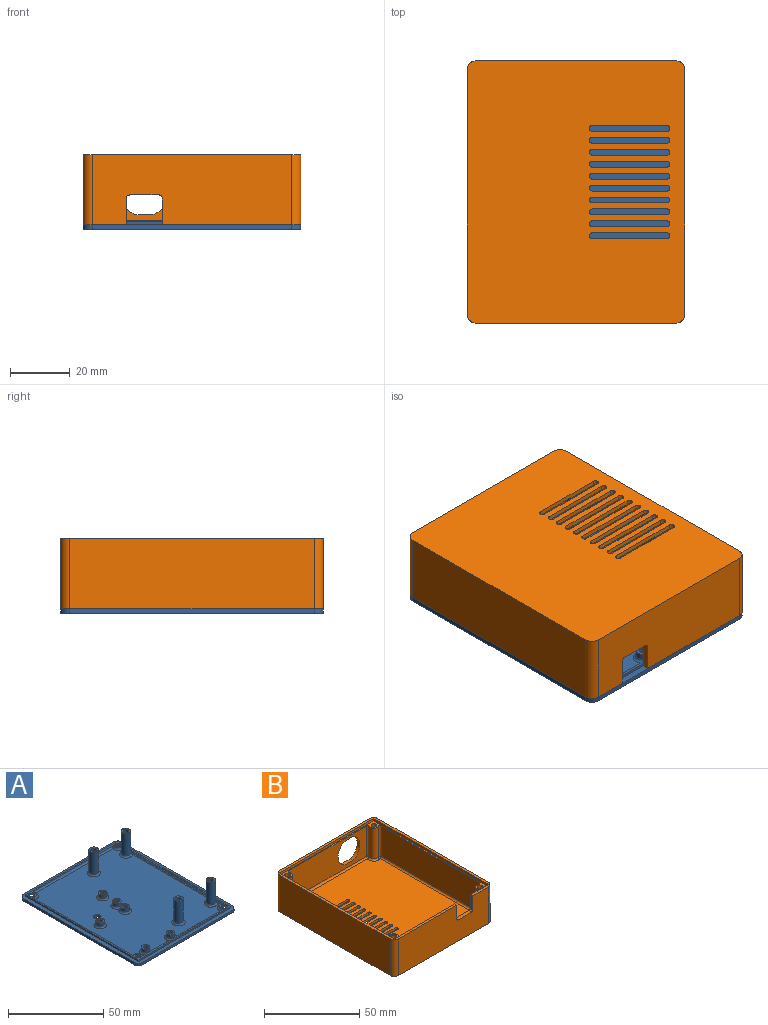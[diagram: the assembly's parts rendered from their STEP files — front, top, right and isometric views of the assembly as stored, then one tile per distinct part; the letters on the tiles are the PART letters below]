
ASSEMBLY  parts=2 mates=1
PART A: 83 faces, bbox 73x88x16.5 mm
  f0: plane 88x73mm, normal (0,0,1), area 620.3mm2, adj f2,f3,f4,f6,f9,f10,f11,f12
  f1: plane 80x65mm, normal (0,0,1), area 4801mm2, adj f5,f57,f58,f59,f60,f61,f62,f63
  f2: plane 82x1.5mm, normal (1,0,0), area 123mm2, adj f0,f7,f53,f56
  f3: plane 67x1.5mm, normal (0,1,0), area 100.5mm2, adj f0,f7,f53,f54
  f4: plane 82x1.5mm, normal (-1,0,0), area 123mm2, adj f0,f7,f54,f55
  f5: cylinder r=2mm len=4mm, axis (0,0,-1), area 18.8mm2, adj f1,f7
  f6: plane 67x1.5mm, normal (0,-1,0), area 100.5mm2, adj f0,f7,f55,f56
  f7: plane 88x73mm, normal (0,0,-1), area 6249.8mm2, adj f2,f3,f4,f5,f6,f53,f54,f55
  f8: plane 84x69mm, normal (0,0,1), area 328.5mm2, adj f9,f10,f11,f12,f57,f58,f59,f62
  f9: plane 84x1mm, normal (-1,0,0), area 84mm2, adj f0,f8,f10,f12
  f10: plane 69x1mm, normal (0,1,0), area 69mm2, adj f0,f8,f9,f11
  f11: plane 84x1mm, normal (1,0,0), area 84mm2, adj f0,f8,f10,f12
  f12: plane 69x1mm, normal (0,-1,0), area 69mm2, adj f0,f8,f9,f11
  f13: plane 4.5x4.5mm, normal (0,0,1), area 11mm2, adj f14,f15
  f14: cylinder r=1.25mm len=3mm, axis (0,0,-1), area 23.6mm2, adj f13,f16
  f15: cylinder r=2.25mm len=4.5mm, axis (0,0,-1), area 28.3mm2, adj f13,f74
  f16: plane 2.5x2.5mm, normal (0,0,1), area 4.9mm2, adj f14
  f17: plane 4.5x4.5mm, normal (0,0,1), area 11mm2, adj f18,f19
  f18: cylinder r=1.25mm len=3mm, axis (0,0,-1), area 23.6mm2, adj f17,f20
  f19: cylinder r=2.25mm len=4.5mm, axis (0,0,-1), area 28.3mm2, adj f17,f71
  f20: plane 2.5x2.5mm, normal (0,0,1), area 4.9mm2, adj f18
  f21: plane 4.5x4.5mm, normal (0,0,1), area 11mm2, adj f22,f23
  f22: cylinder r=1.25mm len=3mm, axis (0,0,-1), area 23.6mm2, adj f21,f24
  f23: cylinder r=2.25mm len=4.5mm, axis (0,0,-1), area 28.3mm2, adj f21,f61
  f24: plane 2.5x2.5mm, normal (0,0,1), area 4.9mm2, adj f22
  f25: plane 4.5x4.5mm, normal (0,0,1), area 11mm2, adj f26,f27
  f26: cylinder r=1.25mm len=3mm, axis (0,0,-1), area 23.6mm2, adj f25,f28
  f27: cylinder r=2.25mm len=4.5mm, axis (0,0,-1), area 28.3mm2, adj f25,f60
  f28: plane 2.5x2.5mm, normal (0,0,1), area 4.9mm2, adj f26
  f29: plane 4.5x4.5mm, normal (0,0,1), area 11mm2, adj f30,f31
  f30: cylinder r=1.25mm len=3mm, axis (0,0,-1), area 23.6mm2, adj f29,f32
  f31: cylinder r=2.25mm len=4.5mm, axis (0,0,-1), area 28.3mm2, adj f29,f73
  f32: plane 2.5x2.5mm, normal (0,0,1), area 4.9mm2, adj f30
  f33: plane 4.5x4.5mm, normal (0,0,1), area 11mm2, adj f34,f35
  f34: cylinder r=1.25mm len=3mm, axis (0,0,-1), area 23.6mm2, adj f33,f36
  f35: cylinder r=2.25mm len=4.5mm, axis (0,0,-1), area 28.3mm2, adj f33,f72
  f36: plane 2.5x2.5mm, normal (0,0,1), area 4.9mm2, adj f34
  f37: plane 5x5mm, normal (0,0,1), area 12.6mm2, adj f38,f39
  f38: cylinder r=1.5mm len=15mm, axis (0,0,-1), area 141.4mm2, adj f37,f40
  f39: cylinder r=2.5mm len=14mm, axis (0,0,-1), area 219.9mm2, adj f37,f70
  f40: plane 3x3mm, normal (0,0,1), area 7.1mm2, adj f38
  f41: plane 5x5mm, normal (0,0,1), area 12.6mm2, adj f42,f43
  f42: cylinder r=1.5mm len=15mm, axis (0,0,-1), area 141.4mm2, adj f41,f44
  f43: cylinder r=2.5mm len=14mm, axis (0,0,-1), area 219.9mm2, adj f41,f64
  f44: plane 3x3mm, normal (0,0,1), area 7.1mm2, adj f42
  f45: plane 5x5mm, normal (0,0,1), area 12.6mm2, adj f46,f47
  f46: cylinder r=1.5mm len=15mm, axis (0,0,-1), area 141.4mm2, adj f45,f48
  f47: cylinder r=2.5mm len=14mm, axis (0,0,-1), area 219.9mm2, adj f45,f69
  f48: plane 3x3mm, normal (0,0,1), area 7.1mm2, adj f46
  f49: plane 5x5mm, normal (0,0,1), area 12.6mm2, adj f50,f51
  f50: cylinder r=1.5mm len=15mm, axis (0,0,-1), area 141.4mm2, adj f49,f52
  f51: cylinder r=2.5mm len=14mm, axis (0,0,-1), area 219.9mm2, adj f49,f68
  f52: plane 3x3mm, normal (0,0,1), area 7.1mm2, adj f50
  f53: cylinder r=3mm len=3mm, axis (0,0,-1), area 7.1mm2, adj f0,f2,f3,f7
  f54: cylinder r=3mm len=3mm, axis (0,0,1), area 7.1mm2, adj f0,f3,f4,f7
  f55: cylinder r=3mm len=3mm, axis (0,0,-1), area 7.1mm2, adj f0,f4,f6,f7
  f56: cylinder r=3mm len=3mm, axis (0,0,1), area 7.1mm2, adj f0,f2,f6,f7
  f57: cylinder r=1mm len=75mm, axis (0,-1,0), area 115.5mm2, adj f1,f8,f58,f59
  f58: torus R=3.5mm, axis (0,0,1), area 10.5mm2, adj f1,f8,f57,f62
  f59: torus R=3.5mm, axis (0,0,1), area 10.5mm2, adj f1,f8,f57,f63
  f60: torus R=3.25mm, axis (0,0,1), area 22mm2, adj f1,f27,f63
  f61: torus R=3.25mm, axis (0,0,1), area 22mm2, adj f1,f23,f63
  f62: cylinder r=1mm len=60mm, axis (-1,0,0), area 91.9mm2, adj f1,f8,f58,f65
  f63: cylinder r=1mm len=60mm, axis (1,0,0), area 85.1mm2, adj f1,f8,f59,f60,f61,f66
  f64: torus R=3.5mm, axis (0,0,1), area 26.9mm2, adj f1,f43,f67
  f65: torus R=3.5mm, axis (0,0,1), area 10.5mm2, adj f1,f8,f62,f67
  f66: torus R=3.5mm, axis (0,0,1), area 10.5mm2, adj f1,f8,f63,f67
  f67: cylinder r=1mm len=75mm, axis (0,1,0), area 112.9mm2, adj f1,f8,f64,f65,f66,f68
  f68: torus R=3.5mm, axis (0,0,1), area 26.9mm2, adj f1,f51,f67
  f69: torus R=3.5mm, axis (0,0,1), area 28.3mm2, adj f1,f47
  f70: torus R=3.5mm, axis (0,0,1), area 28.3mm2, adj f1,f39
  f71: torus R=3.25mm, axis (0,0,1), area 25.7mm2, adj f1,f19,f72
  f72: torus R=3.25mm, axis (0,0,1), area 25.7mm2, adj f1,f35,f71
  f73: torus R=3.25mm, axis (0,0,1), area 25.8mm2, adj f1,f31
  f74: torus R=3.25mm, axis (0,0,1), area 25.8mm2, adj f1,f15
  f75: cylinder r=1.55mm len=3.1mm, axis (0,0,-1), area 2.5mm2, adj f8,f76
  f76: cone r=1.55mm half-angle=41deg, axis (0,0,-1), area 47.2mm2, adj f7,f75
  f77: cylinder r=1.55mm len=3.1mm, axis (0,0,-1), area 2.5mm2, adj f8,f78
  f78: cone r=1.55mm half-angle=41deg, axis (0,0,-1), area 47.2mm2, adj f7,f77
  f79: cylinder r=1.55mm len=3.1mm, axis (0,0,-1), area 2.5mm2, adj f8,f80
  f80: cone r=1.55mm half-angle=41deg, axis (0,0,-1), area 47.2mm2, adj f7,f79
  f81: cylinder r=1.55mm len=3.1mm, axis (0,0,-1), area 2.5mm2, adj f8,f82
  f82: cone r=1.55mm half-angle=41deg, axis (0,0,-1), area 47.2mm2, adj f7,f81
PART B: 106 faces, bbox 73x88x23.5 mm
  f0: plane 88x73mm, normal (0,0,-1), area 5884.9mm2, adj f7,f8,f9,f10,f33,f34,f35,f36
  f1: plane 82x67mm, normal (0,0,1), area 4874.4mm2, adj f45,f48,f49,f52,f53,f56,f57,f60
  f2: plane 88x73mm, normal (0,0,1), area 448.3mm2, adj f3,f4,f7,f8,f9,f10,f11,f12
  f3: plane 13x1.5mm, normal (0,1,0), area 19.5mm2, adj f2,f6,f13,f61
  f4: plane 45x1.5mm, normal (0,1,0), area 67.5mm2, adj f2,f6,f11,f62
  f5: plane 57.68x19.5mm, normal (0,1,0), area 1023.1mm2, adj f6,f37,f44,f45,f61,f62,f63,f64
  f6: plane 85x70mm, normal (0,0,1), area 211.7mm2, adj f3,f4,f5,f11,f12,f13,f14,f15
  f7: plane 82x23.5mm, normal (1,0,0), area 1927mm2, adj f0,f2,f33,f36
  f8: plane 67x23.5mm, normal (0,1,0), area 1370.9mm2, adj f0,f2,f29,f30,f31,f32,f33,f34
  f9: plane 82x23.5mm, normal (-1,0,0), area 1927mm2, adj f0,f2,f34,f35
  f10: plane 67x23.5mm, normal (0,-1,0), area 1454.9mm2, adj f0,f2,f35,f36,f61,f62,f63,f64
  f11: plane 85x1.5mm, normal (1,0,0), area 127.5mm2, adj f2,f4,f6,f12
  f12: plane 70x1.5mm, normal (0,-1,0), area 105mm2, adj f2,f6,f11,f13
  f13: plane 85x1.5mm, normal (-1,0,0), area 127.5mm2, adj f2,f3,f6,f12
  f14: cylinder r=1.5mm len=20.5mm, axis (0,0,-1), area 193.2mm2, adj f6,f28
  f15: cylinder r=1.5mm len=20.5mm, axis (0,0,-1), area 193.2mm2, adj f6,f27
  f16: cylinder r=2.5mm len=19.5mm, axis (0,0,-1), area 119.8mm2, adj f6,f43,f44,f48
  f17: plane 72.68x19.5mm, normal (-1,0,0), area 1417.2mm2, adj f6,f42,f43,f52
  f18: cylinder r=2.5mm len=19.5mm, axis (0,0,-1), area 119.8mm2, adj f6,f41,f42,f56
  f19: plane 57.68x19.5mm, normal (0,-1,0), area 921mm2, adj f6,f29,f30,f31,f32,f40,f41,f60
  f20: cylinder r=2.5mm len=19.5mm, axis (0,0,-1), area 119.8mm2, adj f6,f39,f40,f57
  f21: plane 72.68x19.5mm, normal (1,0,0), area 1417.2mm2, adj f6,f38,f39,f53
  f22: cylinder r=2.5mm len=19.5mm, axis (0,0,-1), area 119.8mm2, adj f6,f37,f38,f49
  f23: cylinder r=1.5mm len=20.5mm, axis (0,0,-1), area 193.2mm2, adj f6,f26
  f24: cylinder r=1.5mm len=20.5mm, axis (0,0,-1), area 193.2mm2, adj f6,f25
  f25: plane 3x3mm, normal (0,0,1), area 7.1mm2, adj f24
  f26: plane 3x3mm, normal (0,0,1), area 7.1mm2, adj f23
  f27: plane 3x3mm, normal (0,0,1), area 7.1mm2, adj f15
  f28: plane 3x3mm, normal (0,0,1), area 7.1mm2, adj f14
  f29: cylinder r=8.12mm len=15.25mm, axis (0,1,0), area 39.6mm2, adj f8,f19,f30,f31
  f30: plane 5.61x2mm, normal (0,0,1), area 11.2mm2, adj f8,f19,f29,f32
  f31: plane 5.61x2mm, normal (0,0,-1), area 11.2mm2, adj f8,f19,f29,f32
  f32: cylinder r=8.12mm len=15.25mm, axis (0,1,0), area 39.6mm2, adj f8,f19,f30,f31
  f33: cylinder r=3mm len=23.5mm, axis (0,0,-1), area 110.7mm2, adj f0,f2,f7,f8
  f34: cylinder r=3mm len=23.5mm, axis (0,0,1), area 110.7mm2, adj f0,f2,f8,f9
  f35: cylinder r=3mm len=23.5mm, axis (0,0,-1), area 110.7mm2, adj f0,f2,f9,f10
  f36: cylinder r=3mm len=23.5mm, axis (0,0,1), area 110.7mm2, adj f0,f2,f7,f10
  f37: cylinder r=1mm len=19.5mm, axis (0,0,-1), area 39.3mm2, adj f5,f6,f22,f47
  f38: cylinder r=1mm len=19.5mm, axis (0,0,-1), area 39.3mm2, adj f6,f21,f22,f51
  f39: cylinder r=1mm len=19.5mm, axis (0,0,-1), area 39.3mm2, adj f6,f20,f21,f55
  f40: cylinder r=1mm len=19.5mm, axis (0,0,-1), area 39.3mm2, adj f6,f19,f20,f59
  f41: cylinder r=1mm len=19.5mm, axis (0,0,-1), area 39.3mm2, adj f6,f18,f19,f58
  f42: cylinder r=1mm len=19.5mm, axis (0,0,-1), area 39.3mm2, adj f6,f17,f18,f54
  f43: cylinder r=1mm len=19.5mm, axis (0,0,-1), area 39.3mm2, adj f6,f16,f17,f50
  f44: cylinder r=1mm len=19.5mm, axis (0,0,-1), area 39.3mm2, adj f5,f6,f16,f46
  f45: cylinder r=1mm len=57.68mm, axis (1,0,0), area 90.6mm2, adj f1,f5,f46,f47
  f46: sphere r=1mm, area 2mm2, adj f44,f45,f48
  f47: sphere r=1mm, area 2mm2, adj f37,f45,f49
  f48: torus R=3.5mm, axis (0,0,1), area 11mm2, adj f1,f16,f46,f50
  f49: torus R=3.5mm, axis (0,0,1), area 11mm2, adj f1,f22,f47,f51
  f50: sphere r=1mm, area 2mm2, adj f43,f48,f52
  f51: sphere r=1mm, area 2mm2, adj f38,f49,f53
  f52: cylinder r=1mm len=72.68mm, axis (0,1,0), area 114.2mm2, adj f1,f17,f50,f54
  f53: cylinder r=1mm len=72.68mm, axis (0,-1,0), area 114.2mm2, adj f1,f21,f51,f55
  f54: sphere r=1mm, area 2mm2, adj f42,f52,f56
  f55: sphere r=1mm, area 2mm2, adj f39,f53,f57
  f56: torus R=3.5mm, axis (0,0,1), area 11mm2, adj f1,f18,f54,f58
  f57: torus R=3.5mm, axis (0,0,1), area 11mm2, adj f1,f20,f55,f59
  f58: sphere r=1mm, area 2mm2, adj f41,f56,f60
  f59: sphere r=1mm, area 2mm2, adj f40,f57,f60
  f60: cylinder r=1mm len=57.68mm, axis (-1,0,0), area 90.6mm2, adj f1,f19,f58,f59
  f61: plane 9x2mm, normal (-1,0,0), area 17.2mm2, adj f2,f3,f5,f6,f10,f65
  f62: plane 9x2mm, normal (1,0,0), area 17.2mm2, adj f2,f4,f5,f6,f10,f64
  f63: plane 10x2mm, normal (0,0,1), area 20mm2, adj f5,f10,f64,f65
  f64: cylinder r=1mm len=2mm, axis (0,1,0), area 3.1mm2, adj f5,f10,f62,f63
  f65: cylinder r=1mm len=2mm, axis (0,1,0), area 3.1mm2, adj f5,f10,f61,f63
  f66: cylinder r=1mm len=2mm, axis (0,0,1), area 4.7mm2, adj f0,f1,f67,f69
  f67: plane 25x1.5mm, normal (0,-1,0), area 37.5mm2, adj f0,f1,f66,f68
  f68: cylinder r=1mm len=2mm, axis (0,0,1), area 4.7mm2, adj f0,f1,f67,f69
  f69: plane 25x1.5mm, normal (0,1,0), area 37.5mm2, adj f0,f1,f66,f68
  f70: cylinder r=1mm len=2mm, axis (0,0,1), area 4.7mm2, adj f0,f1,f71,f73
  f71: plane 25x1.5mm, normal (0,-1,0), area 37.5mm2, adj f0,f1,f70,f72
  f72: cylinder r=1mm len=2mm, axis (0,0,1), area 4.7mm2, adj f0,f1,f71,f73
  f73: plane 25x1.5mm, normal (0,1,0), area 37.5mm2, adj f0,f1,f70,f72
  f74: cylinder r=1mm len=2mm, axis (0,0,1), area 4.7mm2, adj f0,f1,f75,f77
  f75: plane 25x1.5mm, normal (0,-1,0), area 37.5mm2, adj f0,f1,f74,f76
  f76: cylinder r=1mm len=2mm, axis (0,0,1), area 4.7mm2, adj f0,f1,f75,f77
  f77: plane 25x1.5mm, normal (0,1,0), area 37.5mm2, adj f0,f1,f74,f76
  f78: cylinder r=1mm len=2mm, axis (0,0,1), area 4.7mm2, adj f0,f1,f79,f81
  f79: plane 25x1.5mm, normal (0,-1,0), area 37.5mm2, adj f0,f1,f78,f80
  f80: cylinder r=1mm len=2mm, axis (0,0,1), area 4.7mm2, adj f0,f1,f79,f81
  f81: plane 25x1.5mm, normal (0,1,0), area 37.5mm2, adj f0,f1,f78,f80
  f82: cylinder r=1mm len=2mm, axis (0,0,1), area 4.7mm2, adj f0,f1,f83,f85
  f83: plane 25x1.5mm, normal (0,-1,0), area 37.5mm2, adj f0,f1,f82,f84
  f84: cylinder r=1mm len=2mm, axis (0,0,1), area 4.7mm2, adj f0,f1,f83,f85
  f85: plane 25x1.5mm, normal (0,1,0), area 37.5mm2, adj f0,f1,f82,f84
  f86: cylinder r=1mm len=2mm, axis (0,0,1), area 4.7mm2, adj f0,f1,f87,f89
  f87: plane 25x1.5mm, normal (0,-1,0), area 37.5mm2, adj f0,f1,f86,f88
  f88: cylinder r=1mm len=2mm, axis (0,0,1), area 4.7mm2, adj f0,f1,f87,f89
  f89: plane 25x1.5mm, normal (0,1,0), area 37.5mm2, adj f0,f1,f86,f88
  f90: cylinder r=1mm len=2mm, axis (0,0,1), area 4.7mm2, adj f0,f1,f91,f93
  f91: plane 25x1.5mm, normal (0,-1,0), area 37.5mm2, adj f0,f1,f90,f92
  f92: cylinder r=1mm len=2mm, axis (0,0,1), area 4.7mm2, adj f0,f1,f91,f93
  f93: plane 25x1.5mm, normal (0,1,0), area 37.5mm2, adj f0,f1,f90,f92
  f94: cylinder r=1mm len=2mm, axis (0,0,1), area 4.7mm2, adj f0,f1,f95,f97
  f95: plane 25x1.5mm, normal (0,-1,0), area 37.5mm2, adj f0,f1,f94,f96
  f96: cylinder r=1mm len=2mm, axis (0,0,1), area 4.7mm2, adj f0,f1,f95,f97
  f97: plane 25x1.5mm, normal (0,1,0), area 37.5mm2, adj f0,f1,f94,f96
  f98: cylinder r=1mm len=2mm, axis (0,0,1), area 4.7mm2, adj f0,f1,f99,f101
  f99: plane 25x1.5mm, normal (0,-1,0), area 37.5mm2, adj f0,f1,f98,f100
  f100: cylinder r=1mm len=2mm, axis (0,0,1), area 4.7mm2, adj f0,f1,f99,f101
  f101: plane 25x1.5mm, normal (0,1,0), area 37.5mm2, adj f0,f1,f98,f100
  f102: cylinder r=1mm len=2mm, axis (0,0,1), area 4.7mm2, adj f0,f1,f103,f105
  f103: plane 25x1.5mm, normal (0,-1,0), area 37.5mm2, adj f0,f1,f102,f104
  f104: cylinder r=1mm len=2mm, axis (0,0,1), area 4.7mm2, adj f0,f1,f103,f105
  f105: plane 25x1.5mm, normal (0,1,0), area 37.5mm2, adj f0,f1,f102,f104
PLACE A t=(-26.13,5.13,21.08)mm
PLACE B rot(axis=(0,1,0),180deg) t=(-26.13,5.13,46.08)mm
MATE fastened B.f18 <-> A.f58  axis (0,0,1) through (-58.13,44.63,24.08)mm
